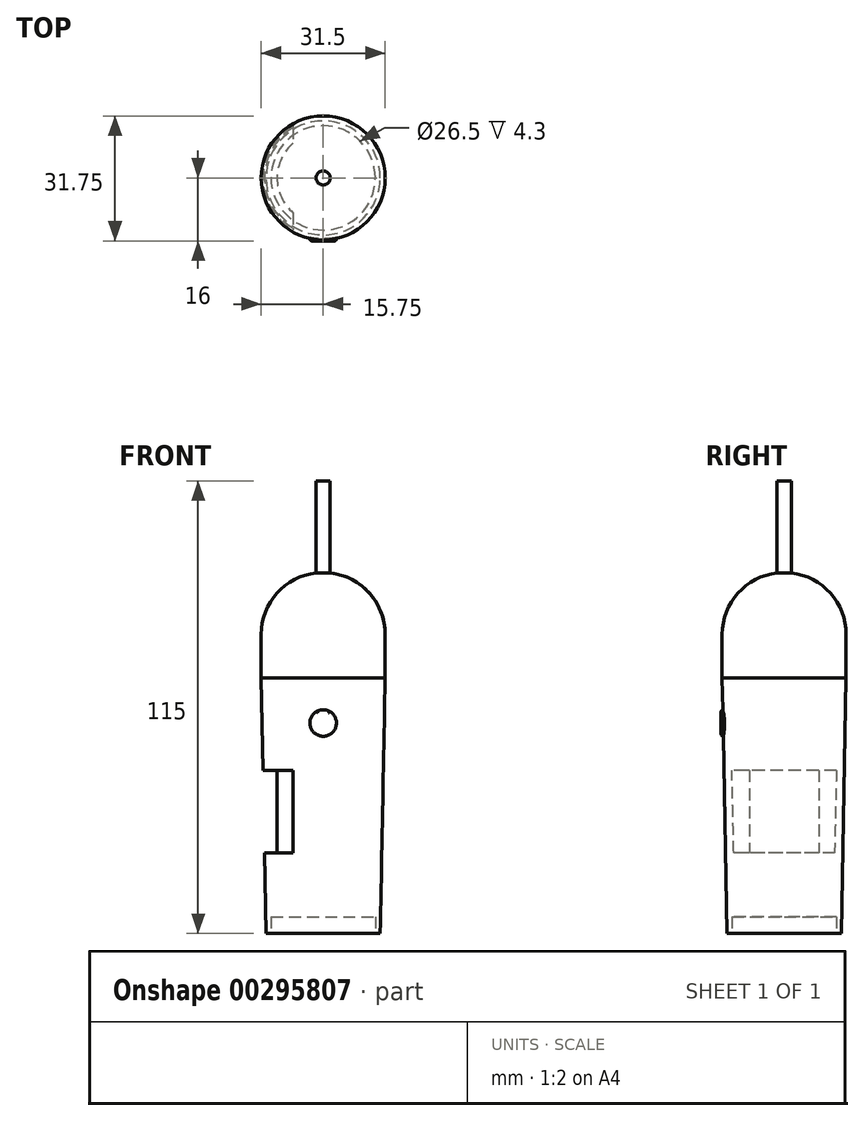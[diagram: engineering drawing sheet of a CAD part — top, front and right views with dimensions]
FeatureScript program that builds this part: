
annotation { "Feature Type Name" : "Feature", "Feature Type Description" : "" }
export const myFeature = defineFeature(function(context is Context, id is Id, definition is map)
    precondition{}
    {
        {
            var Q0;
            Q0=qCreatedBy(makeId("Top.planeOp"),FACE);
            var sketch = newSketch(context, id + "F0", { "sketchPlane" : qUnion([Q0])});
            skCircle(sketch, "E0", {"center": v(0, 0) * mm, "radius": 14.5 * mm});
            skSolve(sketch);
        }
        {
            var Q0;
            Q0=qCreatedBy(makeId("Top.planeOp"),FACE);
            cPlane(context, id + "F1", {"entities" : qUnion([Q0]), "cplaneType" : CPlaneType.OFFSET, "offset" : 65 * mm, "width" : 150 * mm, "height" : 150 * mm});
        }
        {
            var Q0;
            Q0=qCreatedBy(id+"F1.planeOp",FACE);
            var sketch = newSketch(context, id + "F2", { "sketchPlane" : qUnion([Q0])});
            skCircle(sketch, "E1", {"center": v(0, 0) * mm, "radius": 15.75 * mm});
            skSolve(sketch);
        }
        {
            var Q0;
            Q0=makeQuery(id+"F0.imprint","IMPRINT",FACE,{"disambiguationData":[TD([[makeQuery(id+"F0.imprint","IMPRINT",EDGE,{"derivedFrom":sQuery(id+"F0.wireOp",EDGE,"E0")}),1.0]])]});
            var Q1;
            Q1=makeQuery(id+"F2.imprint","IMPRINT",FACE,{"disambiguationData":[TD([[makeQuery(id+"F2.imprint","IMPRINT",EDGE,{"derivedFrom":sQuery(id+"F2.wireOp",EDGE,"E1")}),1.0]])]});
            loft(context, id + "F3", {"sheetProfilesArray" : [{ "sheetProfileEntities" : qUnion([Q0]) }, { "sheetProfileEntities" : qUnion([Q1]) }]});
        }
        {
            var Q0;
            Q0=makeQuery(id+"F3.opLoft","CAP_FACE",FACE,{"disambiguationData":[OSD([makeQuery(id+"F0.imprint","IMPRINT",FACE,{"disambiguationData":[TD([[makeQuery(id+"F0.imprint","IMPRINT",EDGE,{"derivedFrom":sQuery(id+"F0.wireOp",EDGE,"E0")}),1.0]])]})])],"isStart":true});
            var sketch = newSketch(context, id + "F4", { "sketchPlane" : qUnion([Q0])});
            skCircle(sketch, "E2", {"center": v(0, 0) * mm, "radius": 13.25 * mm});
            skSolve(sketch);
        }
        {
            var Q0;
            Q0 = qSketchRegion(id + "F4", true);
            extrude(context, id + "F5", {"entities" : qUnion([Q0]), "operationType" : NewBodyOperationType.REMOVE, "oppositeDirection" : true, "depth" : 4.3 * mm});
        }
        {
            var Q0;
            Q0=qCreatedBy(makeId("Top.planeOp"),FACE);
            cPlane(context, id + "F6", {"entities" : qUnion([Q0]), "cplaneType" : CPlaneType.OFFSET, "offset" : 20.5 * mm, "width" : 150 * mm, "height" : 150 * mm});
        }
        {
            var Q0;
            Q0=qCreatedBy(id+"F6.planeOp",FACE);
            var sketch = newSketch(context, id + "F7", { "sketchPlane" : qUnion([Q0])});
            skArc(sketch, "E3", {"start": v(-7.6, -12.8) * mm, "mid": v(14.9, 0) * mm, "end": v(-7.6, 12.8) * mm});
            skLineSegment(sketch, "E4", {"start": v(-7.6, 12.8) * mm, "end": v(-7.6, -12.8) * mm});
            skCircle(sketch, "E5", {"center": v(0, 0) * mm, "radius": 11.7 * mm});
            skLineSegment(sketch, "E6.bottom", {"start": v(-7.6, 17.92) * mm, "end": v(-23.55, 17.92) * mm});
            skLineSegment(sketch, "E6.top", {"start": v(-7.6, -16.44) * mm, "end": v(-23.55, -16.44) * mm});
            skLineSegment(sketch, "E6.left", {"start": v(-7.6, 17.92) * mm, "end": v(-7.6, -16.44) * mm});
            skLineSegment(sketch, "E6.right", {"start": v(-23.55, 17.92) * mm, "end": v(-23.55, -16.44) * mm});
            skSolve(sketch);
        }
        {
            var Q0;
            {var subQ3=sQuery(id+"F7.wireOp",EDGE,"E6.bottom");Q0=makeQuery(id+"F7.imprint","IMPRINT",FACE,{"disambiguationData":[TD([[makeQuery(id+"F7.imprint","IMPRINT",EDGE,{"derivedFrom":subQ3}),1.0]])]});}
            extrude(context, id + "F8", {"entities" : qUnion([Q0]), "operationType" : NewBodyOperationType.REMOVE, "depth" : 21 * mm});
        }
        {
            var Q0;
            Q0=qCreatedBy(makeId("Front.planeOp"),FACE);
            var sketch = newSketch(context, id + "F9", { "sketchPlane" : qUnion([Q0])});
            skCircle(sketch, "E7", {"center": v(0, 53.5) * mm, "radius": 3.38 * mm});
            skSolve(sketch);
        }
        {
            var Q0;
            Q0 = qSketchRegion(id + "F9", true);
            extrude(context, id + "F10", {"entities" : qUnion([Q0]), "operationType" : NewBodyOperationType.ADD, "depth" : 16 * mm});
        }
        {
            var Q0;
            Q0=makeQuery(id+"F10.opExtrude","CAP_FACE",FACE,{"disambiguationData":[OSD([sQuery(id+"F9.wireOp",EDGE,"E7")])],"isStart":false});
            fillet(context, id + "F11", {"entities" : qUnion([Q0]), "radius" : .5 * mm, "tangentPropagation" : true, "allowEdgeOverflow" : false});
        }
        {
            var Q0;
            Q0=makeQuery(id+"F3.opLoft","CAP_FACE",FACE,{"disambiguationData":[OSD([makeQuery(id+"F2.imprint","IMPRINT",FACE,{"disambiguationData":[TD([[makeQuery(id+"F2.imprint","IMPRINT",EDGE,{"derivedFrom":sQuery(id+"F2.wireOp",EDGE,"E1")}),1.0]])]})])],"isStart":true});
            var sketch = newSketch(context, id + "F12", { "sketchPlane" : qUnion([Q0])});
            skCircle(sketch, "E8", {"center": v(0, 0) * mm, "radius": 15.75 * mm});
            skSolve(sketch);
        }
        {
            var Q0;
            Q0 = qSketchRegion(id + "F12", true);
            extrude(context, id + "F13", {"entities" : qUnion([Q0]), "operationType" : NewBodyOperationType.ADD, "depth" : 11 * mm});
        }
        {
            var Q0;
            Q0=qCreatedBy(makeId("Right.planeOp"),FACE);
            var sketch = newSketch(context, id + "F14", { "sketchPlane" : qUnion([Q0])});
            skLineSegment(sketch, "E9", {"start": v(15.75, 76) * mm, "end": v(-15.75, 76) * mm});
            skLineSegment(sketch, "E10", {"start": v(0, 76) * mm, "end": v(0, 91.75) * mm});
            skArc(sketch, "E11", {"start": v(15.75, 76) * mm, "mid": v(11.14, 87.14) * mm, "end": v(0, 91.75) * mm});
            skSolve(sketch);
        }
        {
            var Q0;
            {var subQ2=sQuery(id+"F14.wireOp",EDGE,"E10");Q0=makeQuery(id+"F14.imprint","IMPRINT",FACE,{"disambiguationData":[TD([[makeQuery(id+"F14.imprint","IMPRINT",EDGE,{"derivedFrom":subQ2}),-1.0]])]});}
            var Q1;
            Q1=sQuery(id+"F14.wireOp",EDGE,"E10");
            revolve(context, id + "F15", {"operationType" : NewBodyOperationType.ADD, "entities" : qUnion([Q0]), "axis" : qUnion([Q1]), "revolveType" : RevolveType.FULL});
        }
        {
            var Q0;
            Q0=qCreatedBy(makeId("Top.planeOp"),FACE);
            cPlane(context, id + "F16", {"entities" : qUnion([Q0]), "cplaneType" : CPlaneType.OFFSET, "offset" : 90 * mm, "width" : 150 * mm, "height" : 150 * mm});
        }
        {
            var Q0;
            Q0=qCreatedBy(id+"F16.planeOp",FACE);
            var sketch = newSketch(context, id + "F17", { "sketchPlane" : qUnion([Q0])});
            skCircle(sketch, "E12", {"center": v(0, 0) * mm, "radius": 1.8 * mm});
            skSolve(sketch);
        }
        {
            var Q0;
            Q0 = qSketchRegion(id + "F17", true);
            extrude(context, id + "F18", {"entities" : qUnion([Q0]), "operationType" : NewBodyOperationType.ADD, "depth" : 25 * mm});
        }
    });
